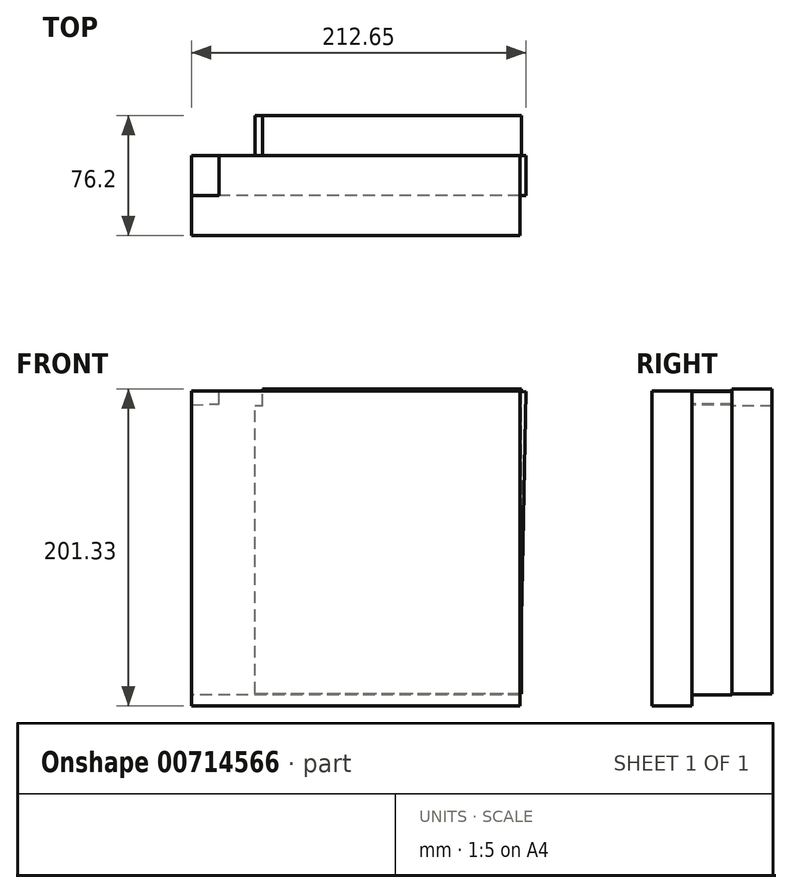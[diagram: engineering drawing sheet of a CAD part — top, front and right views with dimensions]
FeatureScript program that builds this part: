
annotation { "Feature Type Name" : "Feature", "Feature Type Description" : "" }
export const myFeature = defineFeature(function(context is Context, id is Id, definition is map)
    precondition{}
    {
        {
            var Q0;
            Q0=qCreatedBy(makeId("Front.planeOp"),FACE);
            var sketch = newSketch(context, id + "F0", { "sketchPlane" : qUnion([Q0])});
            skLineSegment(sketch, "E0.bottom", {"start": v(74.62, 75.59) * mm, "end": v(-77.7, 75.59) * mm});
            skLineSegment(sketch, "E0.top", {"start": v(74.62, -76.07) * mm, "end": v(-77.7, -76.07) * mm});
            skLineSegment(sketch, "E0.left", {"start": v(74.62, 75.59) * mm, "end": v(74.62, -76.07) * mm});
            skLineSegment(sketch, "E0.right", {"start": v(-77.7, 75.59) * mm, "end": v(-77.7, -76.07) * mm});
            skLineSegment(sketch, "E1.bottom", {"start": v(94.93, -97.13) * mm, "end": v(-96.16, -97.13) * mm});
            skLineSegment(sketch, "E1.top", {"start": v(94.93, 95.76) * mm, "end": v(-96.16, 95.76) * mm});
            skLineSegment(sketch, "E1.left", {"start": v(94.93, -97.13) * mm, "end": v(94.93, 95.76) * mm});
            skLineSegment(sketch, "E1.right", {"start": v(-96.16, -97.13) * mm, "end": v(-96.16, 95.76) * mm});
            skLineSegment(sketch, "E2", {"start": v(0, 11.12) * mm, "end": v(74.62, 11.12) * mm});
            skLineSegment(sketch, "E3", {"start": v(74.62, 11.12) * mm, "end": v(81.6, -13.41) * mm});
            skLineSegment(sketch, "E4", {"start": v(81.6, -13.41) * mm, "end": v(-77.7, -8.76) * mm});
            skLineSegment(sketch, "E5", {"start": v(-77.7, -8.76) * mm, "end": v(-77.7, 12.52) * mm});
            skLineSegment(sketch, "E6", {"start": v(-77.7, 12.52) * mm, "end": v(15.29, 11.12) * mm});
            skLineSegment(sketch, "E7", {"start": v(15.29, 11.12) * mm, "end": v(0, 11.12) * mm});
            skLineSegment(sketch, "E8", {"start": v(0, 11.12) * mm, "end": v(0, 75.59) * mm});
            skLineSegment(sketch, "E9", {"start": v(0, 75.59) * mm, "end": v(0, -11.09) * mm});
            skPoint(sketch, "E9.endSnap0", {"position": v(1.95, -11.09) * mm});
            skLineSegment(sketch, "E10", {"start": v(0, -11.09) * mm, "end": v(0, -76.07) * mm});
            skSolve(sketch);
        }
        {
            var Q0;
            Q0 = qSketchRegion(id + "F0", true);
            extrude(context, id + "F1", {"entities" : qUnion([Q0]), "depth" : 25.4 * mm, "offsetDistance" : 25.4 * mm});
        }
        {
            var Q0;
            Q0=makeQuery(id+"F1.opExtrude","SWEPT_FACE",FACE,{"disambiguationData":[OSD([sQuery(id+"F0.wireOp",EDGE,"E3")])]});
            var sketch = newSketch(context, id + "F2", { "sketchPlane" : qUnion([Q0])});
            skLineSegment(sketch, "E11.bottom", {"start": v(0, -9.74) * mm, "end": v(25.4, -9.74) * mm});
            skLineSegment(sketch, "E11.top", {"start": v(0, -35.25) * mm, "end": v(25.4, -35.25) * mm});
            skLineSegment(sketch, "E11.left", {"start": v(0, -9.74) * mm, "end": v(0, -35.25) * mm});
            skLineSegment(sketch, "E11.right", {"start": v(25.4, -9.74) * mm, "end": v(25.4, -35.25) * mm});
            skSolve(sketch);
        }
        {
            var Q0;
            Q0 = qSketchRegion(id + "F2", true);
            extrude(context, id + "F3", {"entities" : qUnion([Q0]), "operationType" : NewBodyOperationType.ADD, "depth" : 25.4 * mm, "offsetDistance" : 25.4 * mm});
        }
        {
            var Q0;
            Q0=makeQuery(id+"F3.boolean.opBoolean","MERGE",FACE,{"derivedFrom":[makeQuery(id+"F1.opExtrude","CAP_FACE",FACE,{"disambiguationData":[OSD([sQuery(id+"F0.wireOp",EDGE,"E0.bottom"),sQuery(id+"F0.wireOp",EDGE,"E0.top"),sQuery(id+"F0.wireOp",EDGE,"E0.left"),sQuery(id+"F0.wireOp",EDGE,"E0.right"),sQuery(id+"F0.wireOp",EDGE,"E1.bottom"),sQuery(id+"F0.wireOp",EDGE,"E1.top"),sQuery(id+"F0.wireOp",EDGE,"E1.left"),sQuery(id+"F0.wireOp",EDGE,"E1.right"),sQuery(id+"F0.wireOp",EDGE,"E3"),sQuery(id+"F0.wireOp",EDGE,"E4"),sQuery(id+"F0.wireOp",EDGE,"E5")])],"isStart":false}),makeQuery(id+"F3.opExtrude","SWEPT_FACE",FACE,{"disambiguationData":[OSD([sQuery(id+"F2.wireOp",EDGE,"E11.right")])]})]});
            var sketch = newSketch(context, id + "F4", { "sketchPlane" : qUnion([Q0])});
            skLineSegment(sketch, "E12.bottom", {"start": v(94.93, -97.13) * mm, "end": v(-81.78, -97.13) * mm});
            skLineSegment(sketch, "E12.top", {"start": v(94.93, 95.76) * mm, "end": v(-81.78, 95.76) * mm});
            skLineSegment(sketch, "E12.left", {"start": v(94.93, -97.13) * mm, "end": v(94.93, 95.76) * mm});
            skLineSegment(sketch, "E12.right", {"start": v(-81.78, -97.13) * mm, "end": v(-81.78, 95.76) * mm});
            skLineSegment(sketch, "E13.bottom", {"start": v(-30.83, 95.76) * mm, "end": v(-113.72, 95.76) * mm});
            skLineSegment(sketch, "E13.top", {"start": v(-30.83, -104.28) * mm, "end": v(-113.72, -104.28) * mm});
            skLineSegment(sketch, "E13.left", {"start": v(-30.83, 95.76) * mm, "end": v(-30.83, -104.28) * mm});
            skLineSegment(sketch, "E13.right", {"start": v(-113.72, 95.76) * mm, "end": v(-113.72, -104.28) * mm});
            skLineSegment(sketch, "E14.bottom", {"start": v(-30.83, -104.28) * mm, "end": v(94.93, -104.28) * mm});
            skLineSegment(sketch, "E14.top", {"start": v(-30.83, -97.13) * mm, "end": v(94.93, -97.13) * mm});
            skLineSegment(sketch, "E14.left", {"start": v(-30.83, -104.28) * mm, "end": v(-30.83, -97.13) * mm});
            skLineSegment(sketch, "E14.right", {"start": v(94.93, -104.28) * mm, "end": v(94.93, -97.13) * mm});
            skSolve(sketch);
        }
        {
            var Q0;
            Q0 = qSketchRegion(id + "F4", true);
            extrude(context, id + "F5", {"entities" : qUnion([Q0]), "operationType" : NewBodyOperationType.ADD, "depth" : 25.4 * mm, "offsetDistance" : 25.4 * mm});
        }
        {
            var Q0;
            {var subQ0=sQuery(id+"F4.wireOp",EDGE,"E14.bottom");var subQ1=sQuery(id+"F4.wireOp",EDGE,"E13.top");var subQ2=sQuery(id+"F4.wireOp",EDGE,"E14.right");var subQ3=sQuery(id+"F4.wireOp",EDGE,"E12.left");var subQ4=sQuery(id+"F4.wireOp",EDGE,"E13.bottom");var subQ5=sQuery(id+"F4.wireOp",EDGE,"E12.top");var subQ6=sQuery(id+"F4.wireOp",EDGE,"E13.right");Q0=makeQuery(id+"F5.boolean.opBoolean","SPLIT",FACE,{"disambiguationData":[TD([makeQuery(id+"F1.opExtrude","SWEPT_FACE",FACE,{"disambiguationData":[OSD([sQuery(id+"F0.wireOp",EDGE,"E1.bottom")])]})])],"derivedFrom":makeQuery(id+"F5.opExtrude","CAP_FACE",FACE,{"disambiguationData":[OSD([subQ5,subQ3,subQ4,subQ1,subQ6,subQ0,subQ2])],"isStart":true})});}
            var sketch = newSketch(context, id + "F6", { "sketchPlane" : qUnion([Q0])});
            skLineSegment(sketch, "E15", {"start": v(113.72, -104.28) * mm, "end": v(-94.93, -104.28) * mm});
            skLineSegment(sketch, "E16", {"start": v(-94.93, -104.28) * mm, "end": v(-94.93, -97.13) * mm});
            skLineSegment(sketch, "E17", {"start": v(-94.93, -97.13) * mm, "end": v(113.72, -97.13) * mm});
            skLineSegment(sketch, "E18", {"start": v(113.72, -97.13) * mm, "end": v(113.72, 86.97) * mm});
            skLineSegment(sketch, "E19", {"start": v(113.72, 86.97) * mm, "end": v(-98.93, 95.34) * mm});
            skLineSegment(sketch, "E20", {"start": v(-98.93, 95.34) * mm, "end": v(-94.93, -97.13) * mm});
            skSolve(sketch);
        }
        {
            var Q0;
            Q0 = qSketchRegion(id + "F6", true);
            extrude(context, id + "F7", {"entities" : qUnion([Q0]), "operationType" : NewBodyOperationType.ADD, "depth" : 25.4 * mm, "offsetDistance" : 25.4 * mm});
        }
        {
            var Q0;
            Q0=makeQuery(id+"F7.boolean.opBoolean","MERGE",FACE,{"derivedFrom":[makeQuery(id+"F3.boolean.opBoolean","MERGE",FACE,{"derivedFrom":[makeQuery(id+"F1.opExtrude","CAP_FACE",FACE,{"disambiguationData":[OSD([sQuery(id+"F0.wireOp",EDGE,"E0.bottom"),sQuery(id+"F0.wireOp",EDGE,"E0.top"),sQuery(id+"F0.wireOp",EDGE,"E0.left"),sQuery(id+"F0.wireOp",EDGE,"E0.right"),sQuery(id+"F0.wireOp",EDGE,"E1.bottom"),sQuery(id+"F0.wireOp",EDGE,"E1.top"),sQuery(id+"F0.wireOp",EDGE,"E1.left"),sQuery(id+"F0.wireOp",EDGE,"E1.right"),sQuery(id+"F0.wireOp",EDGE,"E3"),sQuery(id+"F0.wireOp",EDGE,"E4"),sQuery(id+"F0.wireOp",EDGE,"E5")])],"isStart":true}),makeQuery(id+"F3.opExtrude","SWEPT_FACE",FACE,{"disambiguationData":[OSD([sQuery(id+"F2.wireOp",EDGE,"E11.left")])]})]}),makeQuery(id+"F7.opExtrude","CAP_FACE",FACE,{"disambiguationData":[OSD([sQuery(id+"F6.wireOp",EDGE,"E17"),sQuery(id+"F6.wireOp",EDGE,"E18"),sQuery(id+"F6.wireOp",EDGE,"E19"),sQuery(id+"F6.wireOp",EDGE,"E20")])],"isStart":false})]});
            var sketch = newSketch(context, id + "F8", { "sketchPlane" : qUnion([Q0])});
            skLineSegment(sketch, "E21.bottom", {"start": v(0, 0) * mm, "end": v(-75.35, 0) * mm});
            skLineSegment(sketch, "E21.top", {"start": v(0, 73.78) * mm, "end": v(-75.35, 73.78) * mm});
            skLineSegment(sketch, "E21.left", {"start": v(0, 0) * mm, "end": v(0, 73.78) * mm});
            skLineSegment(sketch, "E21.right", {"start": v(-75.35, 0) * mm, "end": v(-75.35, 73.78) * mm});
            skLineSegment(sketch, "E22.bottom", {"start": v(0, 73.78) * mm, "end": v(75.23, 73.78) * mm});
            skLineSegment(sketch, "E22.top", {"start": v(0, -76.34) * mm, "end": v(75.23, -76.34) * mm});
            skLineSegment(sketch, "E22.left", {"start": v(0, 73.78) * mm, "end": v(0, -76.34) * mm});
            skLineSegment(sketch, "E22.right", {"start": v(75.23, 73.78) * mm, "end": v(75.23, -76.34) * mm});
            skLineSegment(sketch, "E23.bottom", {"start": v(0, -76.34) * mm, "end": v(-75.35, -76.34) * mm});
            skLineSegment(sketch, "E23.left", {"start": v(0, -76.34) * mm, "end": v(0, 0) * mm});
            skLineSegment(sketch, "E23.right", {"start": v(-75.35, -76.34) * mm, "end": v(-75.35, 0) * mm});
            skSolve(sketch);
        }
        {
            var Q0;
            Q0=makeQuery(id+"F8.imprint","IMPRINT",FACE,{"disambiguationData":[TD([[makeQuery(id+"F8.imprint","IMPRINT",EDGE,{"derivedFrom":sQuery(id+"F8.wireOp",EDGE,"E23.bottom")}),-1.0]])]});
            var sketch = newSketch(context, id + "F9", { "sketchPlane" : qUnion([Q0])});
            skLineSegment(sketch, "E24.bottom", {"start": v(-95.94, -96.48) * mm, "end": v(73.33, -96.48) * mm});
            skLineSegment(sketch, "E24.top", {"start": v(-95.94, 86.42) * mm, "end": v(73.33, 86.42) * mm});
            skLineSegment(sketch, "E24.left", {"start": v(-95.94, -96.48) * mm, "end": v(-95.94, 86.42) * mm});
            skLineSegment(sketch, "E24.right", {"start": v(73.33, -96.48) * mm, "end": v(73.33, 86.42) * mm});
            skLineSegment(sketch, "E25.bottom", {"start": v(-95.94, 86.42) * mm, "end": v(68.37, 86.42) * mm});
            skLineSegment(sketch, "E25.top", {"start": v(-95.94, 97.05) * mm, "end": v(68.37, 97.05) * mm});
            skLineSegment(sketch, "E25.left", {"start": v(-95.94, 86.42) * mm, "end": v(-95.94, 97.05) * mm});
            skLineSegment(sketch, "E25.right", {"start": v(68.37, 86.42) * mm, "end": v(68.37, 97.05) * mm});
            skSolve(sketch);
        }
        {
            var Q0;
            Q0 = qSketchRegion(id + "F9", true);
            extrude(context, id + "F10", {"entities" : qUnion([Q0]), "operationType" : NewBodyOperationType.ADD, "depth" : 25.4 * mm, "offsetDistance" : 25.4 * mm});
        }
    });
